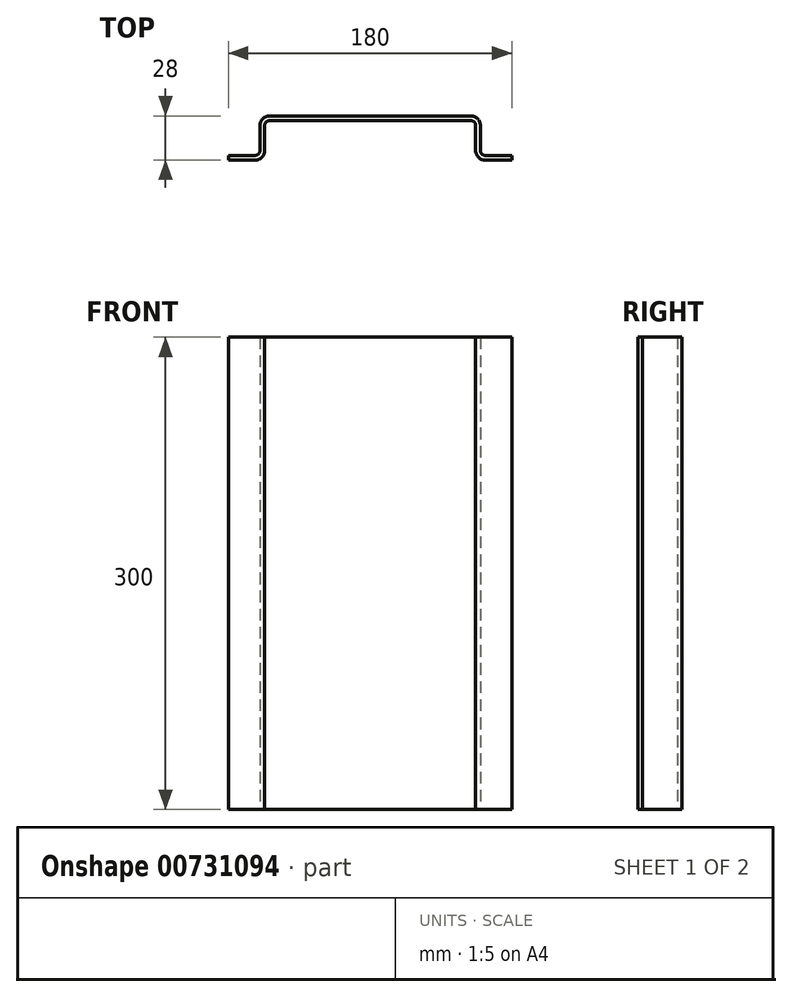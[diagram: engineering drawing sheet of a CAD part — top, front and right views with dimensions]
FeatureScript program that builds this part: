
annotation { "Feature Type Name" : "Feature", "Feature Type Description" : "" }
export const myFeature = defineFeature(function(context is Context, id is Id, definition is map)
    precondition{}
    {
        {
            var Q0;
            Q0=qCreatedBy(makeId("Top.planeOp"),FACE);
            var sketch = newSketch(context, id + "F0", { "sketchPlane" : qUnion([Q0])});
            skLineSegment(sketch, "E0.bottom", {"start": v(-30, 3) * mm, "end": v(110, 3) * mm});
            skLineSegment(sketch, "E0.top", {"start": v(-30, 28) * mm, "end": v(110, 28) * mm});
            skLineSegment(sketch, "E0.left", {"start": v(-30, 3) * mm, "end": v(-30, 28) * mm});
            skLineSegment(sketch, "E0.right", {"start": v(110, 3) * mm, "end": v(110, 28) * mm});
            skLineSegment(sketch, "E1.bottom", {"start": v(-50, 0) * mm, "end": v(130, 0) * mm});
            skLineSegment(sketch, "E1.top", {"start": v(-50, 3) * mm, "end": v(130, 3) * mm});
            skLineSegment(sketch, "E1.left", {"start": v(-50, 0) * mm, "end": v(-50, 3) * mm});
            skLineSegment(sketch, "E1.right", {"start": v(130, 0) * mm, "end": v(130, 3) * mm});
            skSolve(sketch);
        }
        {
            var Q0;
            Q0=makeQuery(id+"F0.imprint","IMPRINT",FACE,{"disambiguationData":[TD([[makeQuery(id+"F0.imprint","IMPRINT",EDGE,{"derivedFrom":sQuery(id+"F0.wireOp",EDGE,"E0.top")}),-1.0]])]});
            var Q1;
            Q1=makeQuery(id+"F0.imprint","IMPRINT",FACE,{"disambiguationData":[TD([[makeQuery(id+"F0.imprint","IMPRINT",EDGE,{"derivedFrom":sQuery(id+"F0.wireOp",EDGE,"E1.bottom")}),1.0]])]});
            extrude(context, id + "F1", {"entities" : qUnion([Q0, Q1]), "endBound" : BoundingType.SYMMETRIC, "depth" : 300 * mm, "offsetDistance" : 25 * mm});
        }
        {
            var Q0;
            Q0=makeQuery(id+"F1.opExtrude","CAP_FACE",FACE,{"disambiguationData":[OSD([sQuery(id+"F0.wireOp",EDGE,"E0.top"),sQuery(id+"F0.wireOp",EDGE,"E0.left"),sQuery(id+"F0.wireOp",EDGE,"E0.right"),sQuery(id+"F0.wireOp",EDGE,"E1.bottom"),sQuery(id+"F0.wireOp",EDGE,"E1.top"),sQuery(id+"F0.wireOp",EDGE,"E1.left"),sQuery(id+"F0.wireOp",EDGE,"E1.right")])],"isStart":false});
            var Q1;
            Q1=makeQuery(id+"F1.opExtrude","CAP_FACE",FACE,{"disambiguationData":[OSD([sQuery(id+"F0.wireOp",EDGE,"E0.top"),sQuery(id+"F0.wireOp",EDGE,"E0.left"),sQuery(id+"F0.wireOp",EDGE,"E0.right"),sQuery(id+"F0.wireOp",EDGE,"E1.bottom"),sQuery(id+"F0.wireOp",EDGE,"E1.top"),sQuery(id+"F0.wireOp",EDGE,"E1.left"),sQuery(id+"F0.wireOp",EDGE,"E1.right")])],"isStart":true});
            var Q2;
            Q2=makeQuery(id+"F1.opExtrude","SWEPT_FACE",FACE,{"disambiguationData":[OSD([sQuery(id+"F0.wireOp",EDGE,"E1.bottom")])]});
            shell(context, id + "F2", {"entities" : qUnion([Q0, Q1, Q2]), "thickness" : 3 * mm});
        }
        {
            var Q0;
            Q0=makeQuery(id+"F1.opExtrude","SWEPT_EDGE",EDGE,{"disambiguationData":[OSD([sQuery(id+"F0.wireOp",EDGE,"E0.left"),sQuery(id+"F0.wireOp",EDGE,"E1.top")])]});
            var Q1;
            Q1=makeQuery(id+"F1.opExtrude","SWEPT_EDGE",EDGE,{"disambiguationData":[OSD([sQuery(id+"F0.wireOp",EDGE,"E0.right"),sQuery(id+"F0.wireOp",EDGE,"E1.top")])]});
            var Q2;
            Q2=makeQuery(id+"F2.opShell","OFFSET_EDGE",EDGE,{"disambiguationData":[OSD([sQuery(id+"F0.wireOp",EDGE,"E0.top"),sQuery(id+"F0.wireOp",EDGE,"E0.left")])]});
            var Q3;
            Q3=makeQuery(id+"F2.opShell","OFFSET_EDGE",EDGE,{"disambiguationData":[OSD([sQuery(id+"F0.wireOp",EDGE,"E0.top"),sQuery(id+"F0.wireOp",EDGE,"E0.right")])]});
            fillet(context, id + "F3", {"entities" : qUnion([Q0, Q1, Q2, Q3]), "radius" : 3 * mm, "tangentPropagation" : true, "allowEdgeOverflow" : false});
        }
        {
            var Q0;
            Q0=makeQuery(id+"F2.opShell","OFFSET_EDGE",EDGE,{"disambiguationData":[OSD([sQuery(id+"F0.wireOp",EDGE,"E0.left"),sQuery(id+"F0.wireOp",EDGE,"E1.top")])]});
            var Q1;
            Q1=makeQuery(id+"F2.opShell","OFFSET_EDGE",EDGE,{"disambiguationData":[OSD([sQuery(id+"F0.wireOp",EDGE,"E0.right"),sQuery(id+"F0.wireOp",EDGE,"E1.top")])]});
            var Q2;
            Q2=makeQuery(id+"F1.opExtrude","SWEPT_EDGE",EDGE,{"disambiguationData":[OSD([sQuery(id+"F0.wireOp",EDGE,"E0.top"),sQuery(id+"F0.wireOp",EDGE,"E0.left")])]});
            var Q3;
            Q3=makeQuery(id+"F1.opExtrude","SWEPT_EDGE",EDGE,{"disambiguationData":[OSD([sQuery(id+"F0.wireOp",EDGE,"E0.top"),sQuery(id+"F0.wireOp",EDGE,"E0.right")])]});
            fillet(context, id + "F4", {"entities" : qUnion([Q0, Q1, Q2, Q3]), "radius" : 6 * mm, "tangentPropagation" : true, "allowEdgeOverflow" : false});
        }
    });
